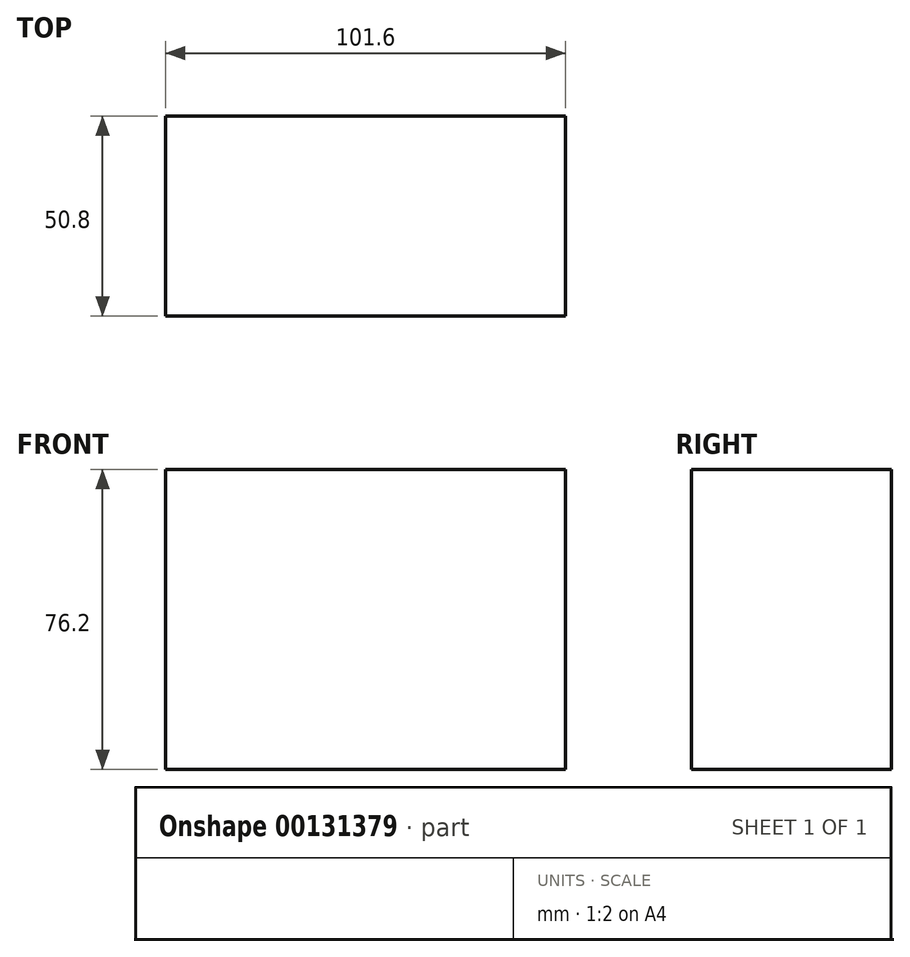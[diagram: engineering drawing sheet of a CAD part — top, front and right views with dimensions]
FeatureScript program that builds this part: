
annotation { "Feature Type Name" : "Feature", "Feature Type Description" : "" }
export const myFeature = defineFeature(function(context is Context, id is Id, definition is map)
    precondition{}
    {
        {
            var Q0;
            Q0=qCreatedBy(makeId("Front.planeOp"),FACE);
            var sketch = newSketch(context, id + "F0", { "sketchPlane" : qUnion([Q0])});
            skLineSegment(sketch, "E0.bottom", {"start": v(50.8, 38.1) * mm, "end": v(-50.8, 38.1) * mm});
            skLineSegment(sketch, "E0.top", {"start": v(50.8, -38.1) * mm, "end": v(-50.8, -38.1) * mm});
            skLineSegment(sketch, "E0.left", {"start": v(50.8, 38.1) * mm, "end": v(50.8, -38.1) * mm});
            skLineSegment(sketch, "E0.right", {"start": v(-50.8, 38.1) * mm, "end": v(-50.8, -38.1) * mm});
            skPoint(sketch, "E0.middle", {"position": v(0, 0) * mm});
            skSolve(sketch);
        }
        {
            var Q0;
            Q0 = qSketchRegion(id + "F0", true);
            extrude(context, id + "F1", {"entities" : qUnion([Q0]), "endBound" : BoundingType.SYMMETRIC, "depth" : 50.8 * mm});
        }
    });
